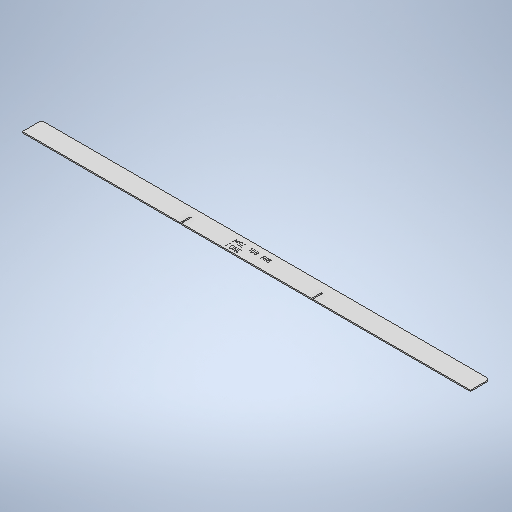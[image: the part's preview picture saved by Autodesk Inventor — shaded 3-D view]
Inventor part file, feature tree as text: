
AUTODESK INVENTOR PART (.ipt)
format: ipt  version: 2025 (Build 290162010, 162A)  size: 380,416 bytes
history: native  units: mm
features: other x5, sketch x3, sheet_metal_op x1, extrude x1
ambient origin geometry x8: Origin, YZ Plane, XZ Plane, XY Plane, X Axis, Y Axis, Z Axis, Center Point
bodies: Body1 (feature_tree)
feature tree (10):
  sheet_metal_op  "Face1"
  extrude  "Extrusion1"  Depth=1170.0mm
  other  "Mark1"
  other  "A-Side Definition"
  other  "Corner Chamfer1"
  sketch  "Sketch1"  dims[d16=50.0mm d17=1170.0mm]
  other  "Plate2"
  sketch  "Sketch2"  dims[d18=50.0mm]
  sketch  "Sketch4"  dims[d19=50.0mm d20=3.0mm d24=0.0mm d25=0.0mm d32=2.0mm d33=8.726646mm d39=26.0mm d41=3.1mm d42=3.0mm d43=340.0mm d45=6.0mm d46=6.0mm d47=45.0deg]
  other  "Definition1"
